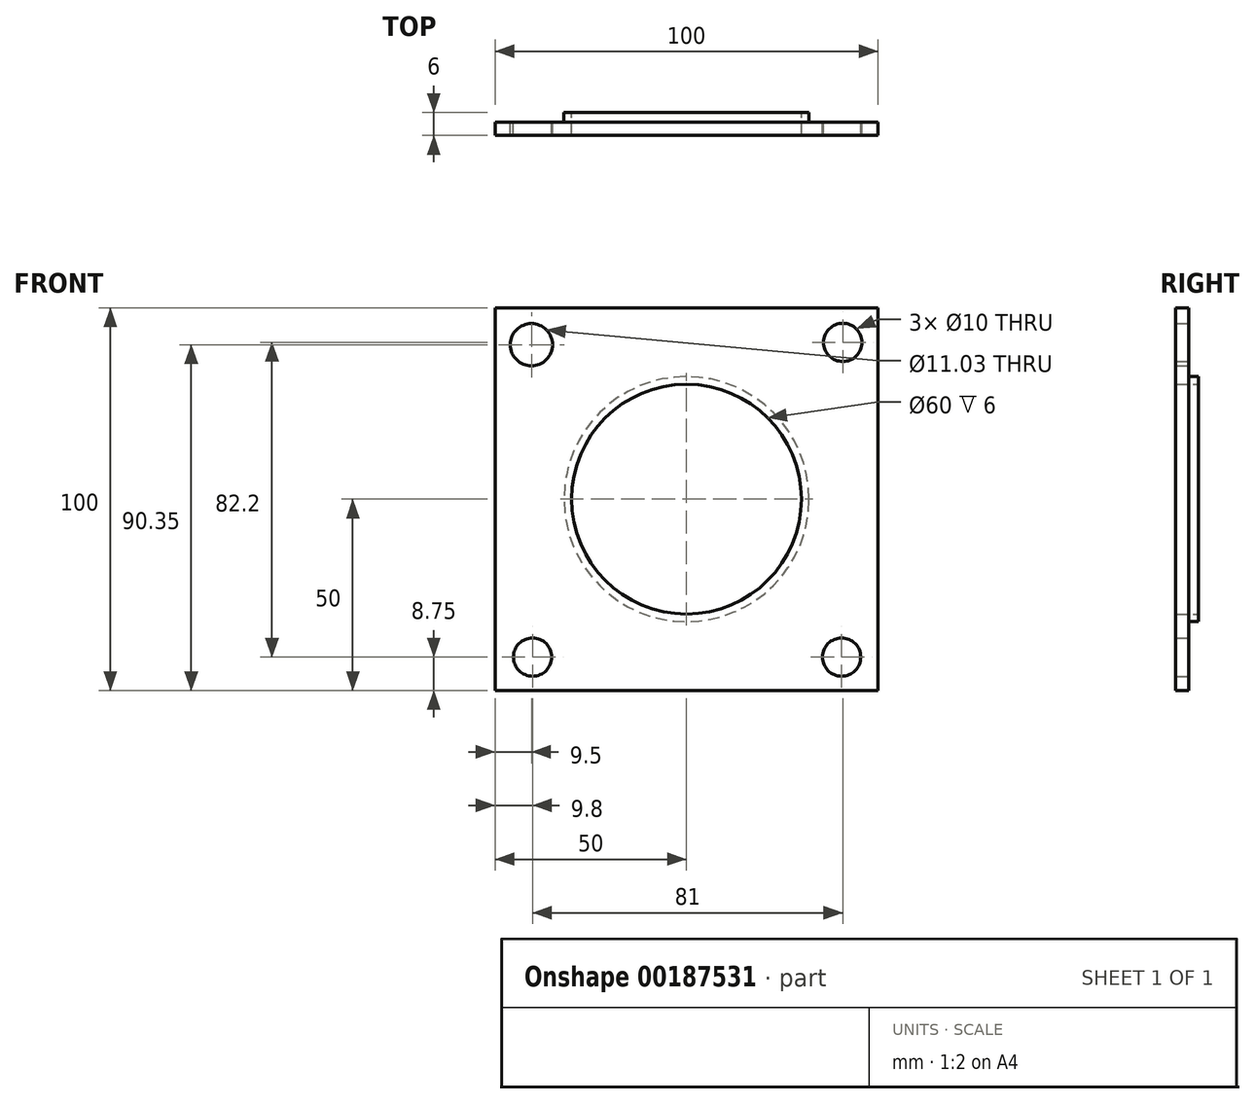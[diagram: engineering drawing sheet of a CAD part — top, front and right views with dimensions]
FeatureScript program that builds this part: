
annotation { "Feature Type Name" : "Feature", "Feature Type Description" : "" }
export const myFeature = defineFeature(function(context is Context, id is Id, definition is map)
    precondition{}
    {
        {
            var Q0;
            Q0=qCreatedBy(makeId("Front.planeOp"),FACE);
            var sketch = newSketch(context, id + "F0", { "sketchPlane" : qUnion([Q0])});
            skLineSegment(sketch, "E0.bottom", {"start": v(-50, 50) * mm, "end": v(50, 50) * mm});
            skLineSegment(sketch, "E0.top", {"start": v(-50, -50) * mm, "end": v(50, -50) * mm});
            skLineSegment(sketch, "E0.left", {"start": v(-50, 50) * mm, "end": v(-50, -50) * mm});
            skLineSegment(sketch, "E0.right", {"start": v(50, 50) * mm, "end": v(50, -50) * mm});
            skPoint(sketch, "E0.middle", {"position": v(0, 0) * mm});
            skCircle(sketch, "E1", {"center": v(0, 0) * mm, "radius": 32 * mm});
            skCircle(sketch, "E2", {"center": v(-40.5, 40.35) * mm, "radius": 5.52 * mm});
            skCircle(sketch, "E3", {"center": v(40.8, 40.95) * mm, "radius": 5 * mm});
            skCircle(sketch, "E4", {"center": v(40.5, -41.25) * mm, "radius": 5 * mm});
            skCircle(sketch, "E5", {"center": v(-40.2, -41.25) * mm, "radius": 5 * mm});
            skSolve(sketch);
        }
        {
            var Q0;
            Q0=makeQuery(id+"F0.imprint","IMPRINT",FACE,{"disambiguationData":[TD([[makeQuery(id+"F0.imprint","IMPRINT",EDGE,{"derivedFrom":sQuery(id+"F0.wireOp",EDGE,"E0.bottom")}),-1.0]])]});
            var Q1;
            Q1=makeQuery(id+"F0.imprint","IMPRINT",FACE,{"disambiguationData":[TD([[makeQuery(id+"F0.imprint","IMPRINT",EDGE,{"derivedFrom":sQuery(id+"F0.wireOp",EDGE,"E1")}),1.0]])]});
            extrude(context, id + "F1", {"entities" : qUnion([Q0, Q1]), "depth" : 2.5 * mm});
        }
        {
            var Q0;
            Q0=makeQuery(id+"F0.imprint","IMPRINT",FACE,{"disambiguationData":[TD([[makeQuery(id+"F0.imprint","IMPRINT",EDGE,{"derivedFrom":sQuery(id+"F0.wireOp",EDGE,"E1")}),1.0]])]});
            var Q1;
            Q1=makeQuery(id+"F1.opExtrude","CAP_FACE",FACE,{"disambiguationData":[OSD([sQuery(id+"F0.wireOp",EDGE,"E0.bottom"),sQuery(id+"F0.wireOp",EDGE,"E0.top"),sQuery(id+"F0.wireOp",EDGE,"E0.left"),sQuery(id+"F0.wireOp",EDGE,"E0.right"),sQuery(id+"F0.wireOp",EDGE,"E2"),sQuery(id+"F0.wireOp",EDGE,"E3"),sQuery(id+"F0.wireOp",EDGE,"E4"),sQuery(id+"F0.wireOp",EDGE,"E5")])],"isStart":false});
            extrude(context, id + "F2", {"entities" : qUnion([Q0, Q1]), "operationType" : NewBodyOperationType.ADD, "oppositeDirection" : true, "depth" : 3.5 * mm});
        }
        {
            var Q0;
            Q0=makeQuery(id+"F2.opExtrude","CAP_FACE",FACE,{"disambiguationData":[OSD([sQuery(id+"F0.wireOp",EDGE,"E1")])],"isStart":false});
            var sketch = newSketch(context, id + "F3", { "sketchPlane" : qUnion([Q0])});
            skCircle(sketch, "E6", {"center": v(0, 0) * mm, "radius": 30 * mm});
            skSolve(sketch);
        }
        {
            var Q0;
            Q0=makeQuery(id+"F3.imprint","IMPRINT",FACE,{"disambiguationData":[TD([[makeQuery(id+"F3.imprint","IMPRINT",EDGE,{"derivedFrom":sQuery(id+"F3.wireOp",EDGE,"E6")}),1.0]])]});
            extrude(context, id + "F4", {"entities" : qUnion([Q0]), "operationType" : NewBodyOperationType.REMOVE, "oppositeDirection" : true, "depth" : 25 * mm});
        }
    });
